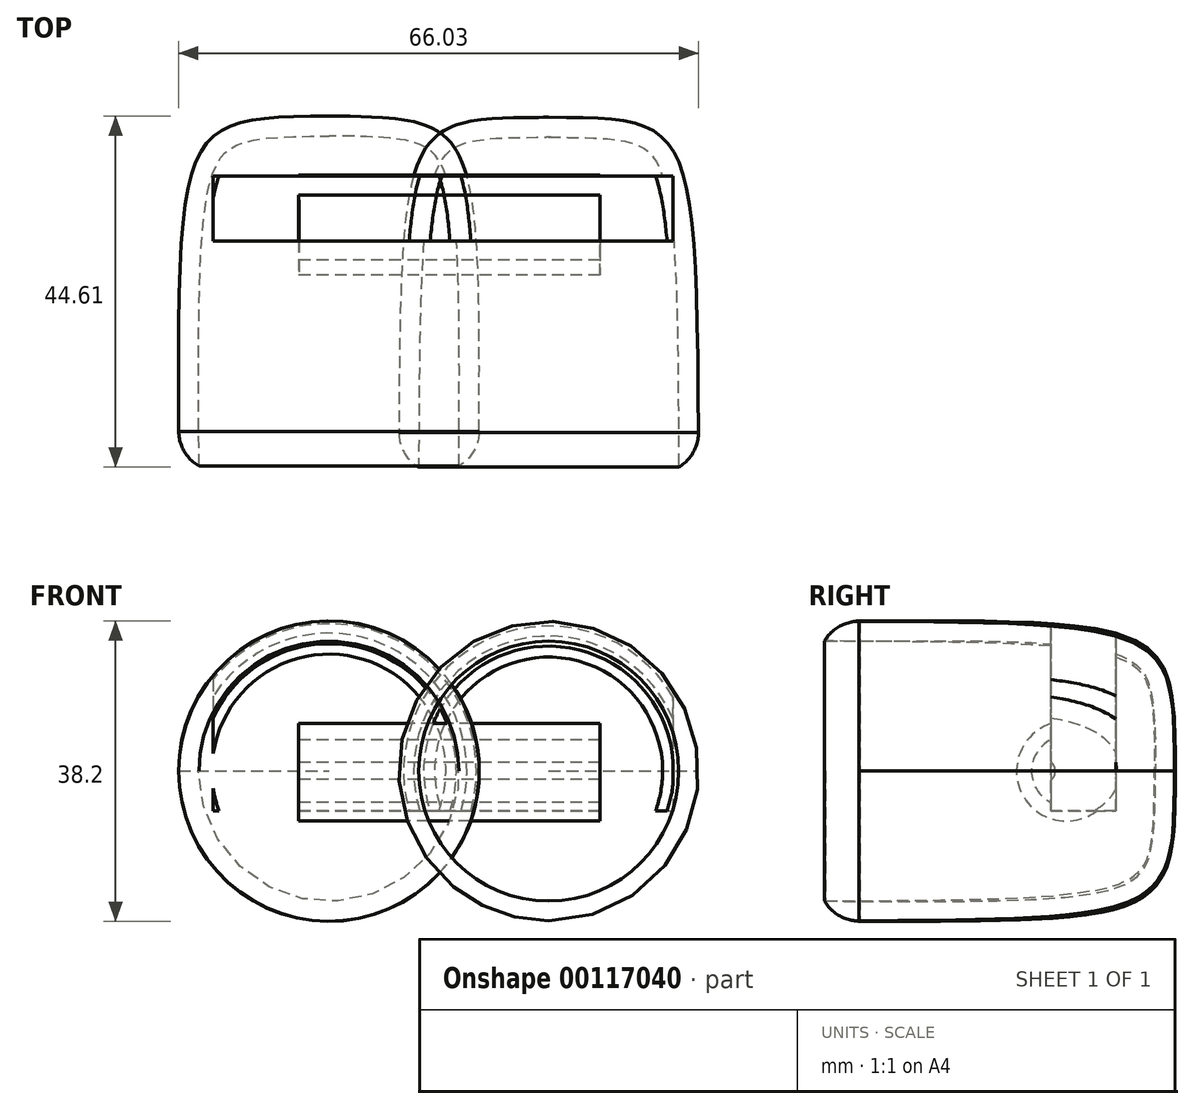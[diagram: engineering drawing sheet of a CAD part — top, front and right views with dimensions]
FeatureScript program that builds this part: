
annotation { "Feature Type Name" : "Feature", "Feature Type Description" : "" }
export const myFeature = defineFeature(function(context is Context, id is Id, definition is map)
    precondition{}
    {
        {
            var Q0;
            Q0=qCreatedBy(makeId("Top.planeOp"),FACE);
            var sketch = newSketch(context, id + "F0", { "sketchPlane" : qUnion([Q0])});
            skPoint(sketch, "E0", {"position": v(12.74, 0) * mm});
            skLineSegment(sketch, "E1", {"start": v(12.74, 0) * mm, "end": v(31.79, 0) * mm});
            skLineSegment(sketch, "E2", {"start": v(-34.22, 0.16) * mm, "end": v(-15.17, 0.16) * mm});
            skLineSegment(sketch, "E3", {"start": v(-15.17, 0.16) * mm, "end": v(-15.17, 44.61) * mm});
            skLineSegment(sketch, "E4", {"start": v(12.74, 0) * mm, "end": v(12.74, 44.45) * mm});
            skFitSpline(sketch, "E5", {"points": [v(12.74, 44.45) * mm, v(31.79, 0) * mm], "startDerivative": vector(56.43, -0.1) * mm, "endDerivative": vector(0.72, -133.24) * mm});
            skFitSpline(sketch, "E6", {"points": [v(-34.22, 0.16) * mm, v(-15.17, 44.61) * mm], "startDerivative": vector(-0.74, 132.76) * mm, "endDerivative": vector(57.89, 0.6) * mm});
            skSolve(sketch);
        }
        {
            var Q0;
            Q0=makeQuery(id+"F0.imprint","IMPRINT",FACE,{"disambiguationData":[TD([[makeQuery(id+"F0.imprint","IMPRINT",EDGE,{"derivedFrom":sQuery(id+"F0.wireOp",EDGE,"E1")}),1.0]])]});
            var Q1;
            Q1=sQuery(id+"F0.wireOp",EDGE,"E4");
            revolve(context, id + "F1", {"entities" : qUnion([Q0]), "axis" : qUnion([Q1]), "revolveType" : RevolveType.FULL});
        }
        {
            var Q0;
            Q0=makeQuery(id+"F0.imprint","IMPRINT",FACE,{"disambiguationData":[TD([[makeQuery(id+"F0.imprint","IMPRINT",EDGE,{"derivedFrom":sQuery(id+"F0.wireOp",EDGE,"E2")}),1.0]])]});
            var Q1;
            Q1=sQuery(id+"F0.wireOp",EDGE,"E3");
            revolve(context, id + "F2", {"entities" : qUnion([Q0]), "axis" : qUnion([Q1]), "revolveType" : RevolveType.FULL});
        }
        {
            var Q0;
            Q0=qCreatedBy(makeId("Top.planeOp"),FACE);
            var sketch = newSketch(context, id + "F3", { "sketchPlane" : qUnion([Q0])});
            skLineSegment(sketch, "E7", {"start": v(-18.81, 30.75) * mm, "end": v(19.29, 30.75) * mm});
            skLineSegment(sketch, "E8", {"start": v(-19, 24.4) * mm, "end": v(19.29, 24.4) * mm});
            skLineSegment(sketch, "E9", {"start": v(-18.81, 30.75) * mm, "end": v(-19, 24.4) * mm});
            skLineSegment(sketch, "E10", {"start": v(19.29, 30.75) * mm, "end": v(19.29, 24.4) * mm});
            skSolve(sketch);
        }
        {
            var Q0;
            Q0 = qSketchRegion(id + "F3", true);
            var Q1;
            Q1=sQuery(id+"F3.wireOp",EDGE,"E7");
            revolve(context, id + "F4", {"entities" : qUnion([Q0]), "axis" : qUnion([Q1]), "revolveType" : RevolveType.FULL});
        }
        {
            var Q0;
            Q0=makeQuery(id+"F4.opRevolve","SWEPT_FACE",FACE,{"disambiguationData":[OSD([sQuery(id+"F3.wireOp",EDGE,"E9")])]});
            var Q1;
            Q1=makeQuery(id+"F4.opRevolve","SWEPT_FACE",FACE,{"disambiguationData":[OSD([sQuery(id+"F3.wireOp",EDGE,"E10")])]});
            var Q2;
            Q2=makeQuery(id+"F4.opRevolve","SWEPT_BODY",BODY,{"disambiguationData":[OSD([sQuery(id+"F3.wireOp",EDGE,"E7"),sQuery(id+"F3.wireOp",EDGE,"E8"),sQuery(id+"F3.wireOp",EDGE,"E9"),sQuery(id+"F3.wireOp",EDGE,"E10")])]});
            shell(context, id + "F5", {"entities" : qUnion([Q0, Q1]), "parts" : qUnion([Q2]), "thickness" : 1.9 * mm});
        }
        {
            var Q0;
            Q0=makeQuery(id+"F1.opRevolve","SWEPT_FACE",FACE,{"disambiguationData":[OSD([sQuery(id+"F0.wireOp",EDGE,"E1")])]});
            var Q1;
            Q1=makeQuery(id+"F2.opRevolve","SWEPT_FACE",FACE,{"disambiguationData":[OSD([sQuery(id+"F0.wireOp",EDGE,"E2")])]});
            shell(context, id + "F6", {"entities" : qUnion([Q0, Q1]), "thickness" : 2.54 * mm});
        }
        {
            var Q0;
            Q0=makeQuery(id+"F2.opRevolve","SWEPT_EDGE",EDGE,{"disambiguationData":[OSD([sQuery(id+"F0.wireOp",EDGE,"E2"),sQuery(id+"F0.wireOp",EDGE,"E6")])]});
            var Q1;
            Q1=makeQuery(id+"F1.opRevolve","SWEPT_EDGE",EDGE,{"disambiguationData":[OSD([sQuery(id+"F0.wireOp",EDGE,"E1"),sQuery(id+"F0.wireOp",EDGE,"E5")])]});
            fillet(context, id + "F7", {"entities" : qUnion([Q0, Q1]), "radius" : 5.08 * mm, "tangentPropagation" : true, "allowEdgeOverflow" : false});
        }
        {
            var Q0;
            Q0=qCreatedBy(makeId("Top.planeOp"),FACE);
            cPlane(context, id + "F8", {"entities" : qUnion([Q0]), "cplaneType" : CPlaneType.OFFSET, "offset" : 5.08 * mm, "oppositeDirection" : true, "width" : 152.4 * mm, "height" : 152.4 * mm});
        }
        {
            var Q0;
            Q0=qCreatedBy(id+"F8.planeOp",FACE);
            var sketch = newSketch(context, id + "F9", { "sketchPlane" : qUnion([Q0])});
            skLineSegment(sketch, "E11.bottom", {"start": v(-29.86, 37) * mm, "end": v(28.56, 37) * mm});
            skLineSegment(sketch, "E11.top", {"start": v(-29.86, 28.75) * mm, "end": v(28.56, 28.75) * mm});
            skLineSegment(sketch, "E11.left", {"start": v(-29.86, 37) * mm, "end": v(-29.86, 28.75) * mm});
            skLineSegment(sketch, "E11.right", {"start": v(28.56, 37) * mm, "end": v(28.56, 28.75) * mm});
            skSolve(sketch);
        }
        {
            var Q0;
            Q0 = qSketchRegion(id + "F9", true);
            extrude(context, id + "F10", {"entities" : qUnion([Q0]), "operationType" : NewBodyOperationType.REMOVE, "depth" : 53.82 * mm});
        }
    });
